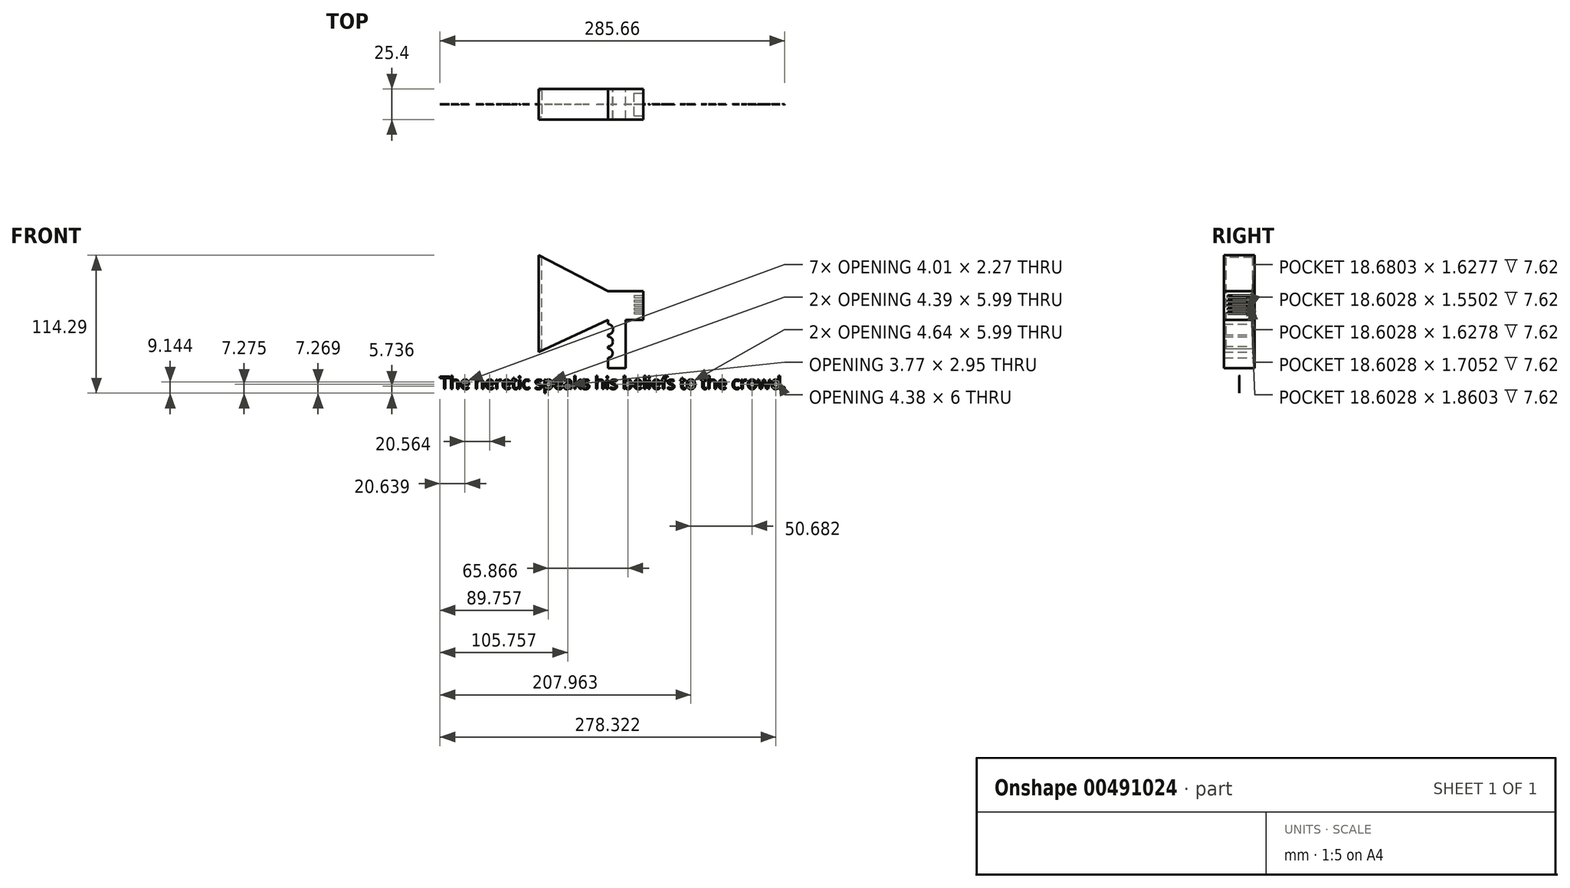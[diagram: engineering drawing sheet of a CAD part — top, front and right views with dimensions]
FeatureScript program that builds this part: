
annotation { "Feature Type Name" : "Feature", "Feature Type Description" : "" }
export const myFeature = defineFeature(function(context is Context, id is Id, definition is map)
    precondition{}
    {
        {
            var Q0;
            Q0=qCreatedBy(makeId("Front.planeOp"),FACE);
            var sketch = newSketch(context, id + "F0", { "sketchPlane" : qUnion([Q0])});
            skLineSegment(sketch, "E0", {"start": v(-5.53, 23.78) * mm, "end": v(23.78, 23.78) * mm});
            skLineSegment(sketch, "E1", {"start": v(23.78, 23.78) * mm, "end": v(23.78, 0) * mm});
            skLineSegment(sketch, "E2", {"start": v(23.78, 0) * mm, "end": v(-5.53, 0) * mm});
            skLineSegment(sketch, "E3", {"start": v(-5.53, 23.78) * mm, "end": v(-5.53, 0) * mm});
            skLineSegment(sketch, "E4", {"start": v(-5.53, 0) * mm, "end": v(-63.05, -26.55) * mm});
            skLineSegment(sketch, "E5", {"start": v(-63.05, -26.55) * mm, "end": v(-63.05, 53.65) * mm});
            skLineSegment(sketch, "E6", {"start": v(-63.05, 53.65) * mm, "end": v(-5.53, 23.78) * mm});
            skLineSegment(sketch, "E7", {"start": v(9.13, 0) * mm, "end": v(9.13, -39.82) * mm});
            skLineSegment(sketch, "E8", {"start": v(9.13, -39.82) * mm, "end": v(-5.53, -39.82) * mm});
            skLineSegment(sketch, "E9", {"start": v(-5.53, -39.82) * mm, "end": v(-5.53, 0) * mm});
            skCircle(sketch, "E10", {"center": v(-5.53, -27.47) * mm, "radius": 3.88 * mm});
            skCircle(sketch, "E11", {"center": v(-5.53, -17.88) * mm, "radius": 4.04 * mm});
            skCircle(sketch, "E12", {"center": v(-5.53, -7.82) * mm, "radius": 4.34 * mm});
            skSolve(sketch);
        }
        {
            var Q0;
            Q0=makeQuery(id+"F0.imprint","IMPRINT",FACE,{"disambiguationData":[TD([[makeQuery(id+"F0.imprint","IMPRINT",EDGE,{"derivedFrom":sQuery(id+"F0.wireOp",EDGE,"E3")}),-1.0]])]});
            var Q1;
            Q1=makeQuery(id+"F0.imprint","IMPRINT",FACE,{"disambiguationData":[TD([[makeQuery(id+"F0.imprint","IMPRINT",EDGE,{"derivedFrom":sQuery(id+"F0.wireOp",EDGE,"E0")}),-1.0]])]});
            var Q2;
            {var subQ7=sQuery(id+"F0.wireOp",EDGE,"E7");Q2=makeQuery(id+"F0.imprint","IMPRINT",FACE,{"disambiguationData":[TD([[makeQuery(id+"F0.imprint","IMPRINT",EDGE,{"derivedFrom":subQ7}),-1.0]])]});}
            extrude(context, id + "F1", {"entities" : qUnion([Q0, Q1, Q2]), "depth" : 12.7 * mm});
        }
        {
            var Q0;
            Q0=makeQuery(id+"F1.opExtrude","CAP_FACE",FACE,{"disambiguationData":[OSD([sQuery(id+"F0.wireOp",EDGE,"E0"),sQuery(id+"F0.wireOp",EDGE,"E1"),sQuery(id+"F0.wireOp",EDGE,"E2"),sQuery(id+"F0.wireOp",EDGE,"E4"),sQuery(id+"F0.wireOp",EDGE,"E5"),sQuery(id+"F0.wireOp",EDGE,"E6"),sQuery(id+"F0.wireOp",EDGE,"E7"),sQuery(id+"F0.wireOp",EDGE,"E8"),sQuery(id+"F0.wireOp",EDGE,"E9"),sQuery(id+"F0.wireOp",EDGE,"E10"),sQuery(id+"F0.wireOp",EDGE,"E11"),sQuery(id+"F0.wireOp",EDGE,"E12")])],"isStart":true});
            extrude(context, id + "F2", {"entities" : qUnion([Q0]), "operationType" : NewBodyOperationType.ADD, "depth" : 12.7 * mm});
        }
        {
            var Q0;
            {var subQ0=sQuery(id+"F0.wireOp",EDGE,"E1");Q0=makeQuery(id+"F2.boolean.opBoolean","MERGE",FACE,{"derivedFrom":[makeQuery(id+"F1.opExtrude","SWEPT_FACE",FACE,{"disambiguationData":[OSD([subQ0])]}),makeQuery(id+"F2.opExtrude","SWEPT_FACE",FACE,{"disambiguationData":[OSD([subQ0])]})]});}
            var sketch = newSketch(context, id + "F3", { "sketchPlane" : qUnion([Q0])});
            skLineSegment(sketch, "E13.bottom", {"start": v(-9.52, 20.43) * mm, "end": v(9.09, 20.43) * mm});
            skLineSegment(sketch, "E13.top", {"start": v(-9.52, 18.57) * mm, "end": v(9.09, 18.57) * mm});
            skLineSegment(sketch, "E13.left", {"start": v(-9.52, 20.43) * mm, "end": v(-9.52, 18.57) * mm});
            skLineSegment(sketch, "E13.right", {"start": v(9.09, 20.43) * mm, "end": v(9.09, 18.57) * mm});
            skLineSegment(sketch, "E14.bottom", {"start": v(-9.52, 16.7) * mm, "end": v(9.09, 16.7) * mm});
            skLineSegment(sketch, "E14.top", {"start": v(-9.52, 15) * mm, "end": v(9.09, 15) * mm});
            skLineSegment(sketch, "E14.left", {"start": v(-9.52, 16.7) * mm, "end": v(-9.52, 15) * mm});
            skLineSegment(sketch, "E14.right", {"start": v(9.09, 16.7) * mm, "end": v(9.09, 15) * mm});
            skLineSegment(sketch, "E15.bottom", {"start": v(-9.52, 12.99) * mm, "end": v(9.09, 12.99) * mm});
            skLineSegment(sketch, "E15.top", {"start": v(-9.52, 11.36) * mm, "end": v(9.09, 11.36) * mm});
            skLineSegment(sketch, "E15.left", {"start": v(-9.52, 12.99) * mm, "end": v(-9.52, 11.36) * mm});
            skLineSegment(sketch, "E15.right", {"start": v(9.09, 12.99) * mm, "end": v(9.09, 11.36) * mm});
            skLineSegment(sketch, "E16.bottom", {"start": v(-9.52, 9.8) * mm, "end": v(9.09, 9.8) * mm});
            skLineSegment(sketch, "E16.top", {"start": v(-9.52, 8.26) * mm, "end": v(9.09, 8.26) * mm});
            skLineSegment(sketch, "E16.left", {"start": v(-9.52, 9.8) * mm, "end": v(-9.52, 8.26) * mm});
            skLineSegment(sketch, "E16.right", {"start": v(9.09, 9.8) * mm, "end": v(9.09, 8.26) * mm});
            skLineSegment(sketch, "E17.bottom", {"start": v(-9.52, 6.7) * mm, "end": v(9.17, 6.7) * mm});
            skLineSegment(sketch, "E17.top", {"start": v(-9.52, 5.08) * mm, "end": v(9.17, 5.08) * mm});
            skLineSegment(sketch, "E17.left", {"start": v(-9.52, 6.7) * mm, "end": v(-9.52, 5.08) * mm});
            skLineSegment(sketch, "E17.right", {"start": v(9.17, 6.7) * mm, "end": v(9.17, 5.08) * mm});
            skSolve(sketch);
        }
        {
            var Q0;
            Q0=makeQuery(id+"F3.imprint","IMPRINT",FACE,{"disambiguationData":[TD([[makeQuery(id+"F3.imprint","IMPRINT",EDGE,{"derivedFrom":sQuery(id+"F3.wireOp",EDGE,"E13.bottom")}),-1.0]])]});
            var Q1;
            Q1=makeQuery(id+"F3.imprint","IMPRINT",FACE,{"disambiguationData":[TD([[makeQuery(id+"F3.imprint","IMPRINT",EDGE,{"derivedFrom":sQuery(id+"F3.wireOp",EDGE,"E14.bottom")}),-1.0]])]});
            var Q2;
            Q2=makeQuery(id+"F3.imprint","IMPRINT",FACE,{"disambiguationData":[TD([[makeQuery(id+"F3.imprint","IMPRINT",EDGE,{"derivedFrom":sQuery(id+"F3.wireOp",EDGE,"E15.bottom")}),-1.0]])]});
            var Q3;
            Q3=makeQuery(id+"F3.imprint","IMPRINT",FACE,{"disambiguationData":[TD([[makeQuery(id+"F3.imprint","IMPRINT",EDGE,{"derivedFrom":sQuery(id+"F3.wireOp",EDGE,"E16.bottom")}),-1.0]])]});
            var Q4;
            Q4=makeQuery(id+"F3.imprint","IMPRINT",FACE,{"disambiguationData":[TD([[makeQuery(id+"F3.imprint","IMPRINT",EDGE,{"derivedFrom":sQuery(id+"F3.wireOp",EDGE,"E17.bottom")}),-1.0]])]});
            extrude(context, id + "F4", {"entities" : qUnion([Q0, Q1, Q2, Q3, Q4]), "operationType" : NewBodyOperationType.REMOVE, "oppositeDirection" : true, "depth" : 7.62 * mm});
        }
        {
            var Q0;
            {var subQ0=sQuery(id+"F0.wireOp",EDGE,"E5");Q0=makeQuery(id+"F2.boolean.opBoolean","MERGE",FACE,{"derivedFrom":[makeQuery(id+"F1.opExtrude","SWEPT_FACE",FACE,{"disambiguationData":[OSD([subQ0])]}),makeQuery(id+"F2.opExtrude","SWEPT_FACE",FACE,{"disambiguationData":[OSD([subQ0])]})]});}
            var sketch = newSketch(context, id + "F5", { "sketchPlane" : qUnion([Q0])});
            skLineSegment(sketch, "E18.bottom", {"start": v(-11.08, -23.98) * mm, "end": v(10.82, -23.98) * mm});
            skLineSegment(sketch, "E18.top", {"start": v(-11.08, 51.7) * mm, "end": v(10.82, 51.7) * mm});
            skLineSegment(sketch, "E18.left", {"start": v(-11.08, -23.98) * mm, "end": v(-11.08, 51.7) * mm});
            skLineSegment(sketch, "E18.right", {"start": v(10.82, -23.98) * mm, "end": v(10.82, 51.7) * mm});
            skSolve(sketch);
        }
        {
            var Q0;
            Q0=makeQuery(id+"F5.imprint","IMPRINT",FACE,{"disambiguationData":[TD([[makeQuery(id+"F5.imprint","IMPRINT",EDGE,{"derivedFrom":sQuery(id+"F5.wireOp",EDGE,"E18.bottom")}),1.0]])]});
            extrude(context, id + "F6", {"entities" : qUnion([Q0]), "operationType" : NewBodyOperationType.REMOVE, "oppositeDirection" : true, "depth" : 2.54 * mm});
        }
        {
            var Q0;
            Q0=qCreatedBy(makeId("Front.planeOp"),FACE);
            var sketch = newSketch(context, id + "F7", { "sketchPlane" : qUnion([Q0])});
            skText(sketch, "E19", { "text": "The heretic speaks his beliefs to the crowd.", "fontName": "OpenSans-Regular.ttf"});
            const initialGuessF7  = {"E19": [-0.14483, -0.0572, 1, 0, 0.01032]};
            skSetInitialGuess(sketch, initialGuessF7);
            skSolve(sketch);
        }
        {
            var Q0;
            Q0 = qSketchRegion(id + "F7", true);
            extrude(context, id + "F8", {"entities" : qUnion([Q0]), "depth" : 0.05 * mm});
        }
    });
